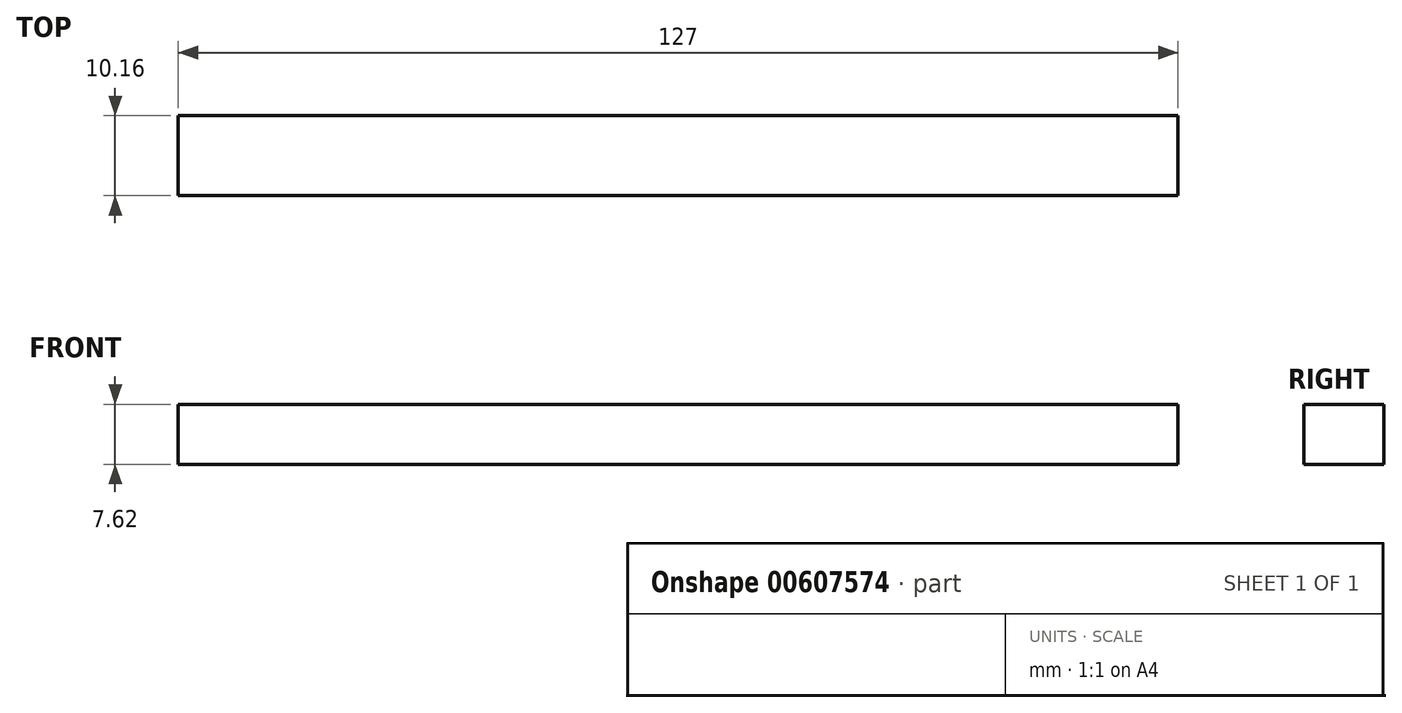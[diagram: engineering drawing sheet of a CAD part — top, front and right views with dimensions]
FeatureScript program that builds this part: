
annotation { "Feature Type Name" : "Feature", "Feature Type Description" : "" }
export const myFeature = defineFeature(function(context is Context, id is Id, definition is map)
    precondition{}
    {
        {
            var Q0;
            Q0=qCreatedBy(makeId("Front.planeOp"),FACE);
            var sketch = newSketch(context, id + "F0", { "sketchPlane" : qUnion([Q0])});
            skLineSegment(sketch, "E0.bottom", {"start": v(-63.5, -3.81) * mm, "end": v(63.5, -3.81) * mm});
            skLineSegment(sketch, "E0.top", {"start": v(-63.5, 3.81) * mm, "end": v(63.5, 3.81) * mm});
            skLineSegment(sketch, "E0.left", {"start": v(-63.5, -3.81) * mm, "end": v(-63.5, 3.81) * mm});
            skLineSegment(sketch, "E0.right", {"start": v(63.5, -3.81) * mm, "end": v(63.5, 3.81) * mm});
            skPoint(sketch, "E0.middle", {"position": v(0, 0) * mm});
            skSolve(sketch);
        }
        {
            var Q0;
            Q0=makeQuery(id+"F0.imprint","IMPRINT",FACE,{"disambiguationData":[TD([[makeQuery(id+"F0.imprint","IMPRINT",EDGE,{"derivedFrom":sQuery(id+"F0.wireOp",EDGE,"E0.bottom")}),1.0]])]});
            extrude(context, id + "F1", {"entities" : qUnion([Q0]), "depth" : 10.16 * mm, "offsetDistance" : 25.4 * mm});
        }
    });
